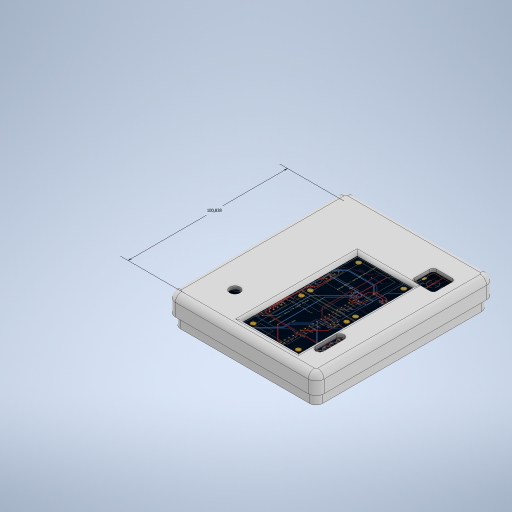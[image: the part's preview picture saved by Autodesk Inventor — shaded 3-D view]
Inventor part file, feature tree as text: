
AUTODESK INVENTOR PART (.ipt)
format: ipt  version: 2024.4 (Build 284460000, 460)  size: 843,776 bytes
history: native  units: mm
features: fillet x7, sketch x5, extrude x4, other x1
ambient origin geometry x8: Origin, YZ Plane, XZ Plane, XY Plane, X Axis, Y Axis, Z Axis, Center Point
bodies: Solid1 (feature_tree)
feature tree (17):
  sketch  "Sketch1"  dims[d3=100.838mm d8=2.12mm]
  extrude  "Extrusion1"  Depth=2.12mm
  extrude  "Extrusion2"  Depth=3.88mm
  extrude  "Extrusion3"  Depth=10.0mm TaperAngle=0.0deg
  fillet  "Fillet3"  Radius=2.0mm
  fillet  "Fillet4"  Radius=2.0mm
  fillet  "Fillet5"  Radius=4.0mm
  extrude  "Extrusion4"  Depth=2.0mm
  fillet  "Fillet6"  Radius=2.0mm
  fillet  "Fillet7"  Radius=2.0mm
  fillet  "Fillet8"  Radius=4.0mm
  fillet  "Fillet9"  Radius=4.0mm
  other  "Image1"
  sketch  "Sketch2"  dims[d9=3.88mm d10=3.88mm]
  sketch  "Sketch3"  dims[d11=2.12mm d12=10.0mm d13=0.0mm d14=2.0mm d15=0.0mm d16=2.0mm d17=0.0mm d20=4.0mm]
  sketch  "Sketch4"  dims[d22=2.6mm d23=2.0mm d24=2.0mm d25=2.0mm]
  sketch  "Sketch6"  dims[d26=7.0mm d27=10.0mm d28=0.0mm d29=0.0mm d30=4.0mm d31=4.0mm d32=2.0mm d33=5.0mm d34=6.5mm d39=94.030423mm d40=112.838mm d35=0.0mm d36=0.0mm]
